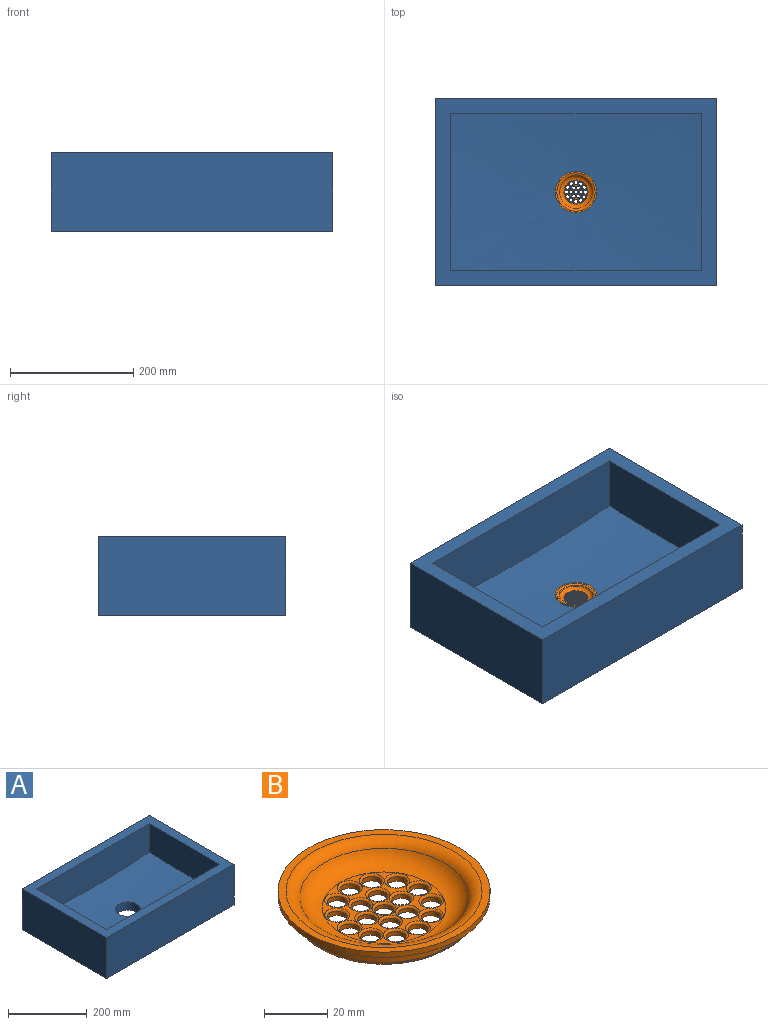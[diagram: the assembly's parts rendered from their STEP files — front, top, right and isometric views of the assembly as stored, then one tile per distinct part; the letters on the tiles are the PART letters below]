
ASSEMBLY  parts=2 mates=1
PART A: 12 faces, bbox 479x479x127 mm
  f0: plane 457.2x304.8mm, normal (0,0,1), area 36129mm2, adj f1,f2,f3,f4,f7,f8,f9,f10
  f1: plane 304.8x127mm, normal (1,0,0), area 38709.6mm2, adj f0,f2,f4,f6
  f2: plane 457.2x127mm, normal (0,1,0), area 58064.4mm2, adj f0,f1,f3,f6
  f3: plane 304.8x127mm, normal (-1,0,0), area 38709.6mm2, adj f0,f2,f4,f6
  f4: plane 457.2x127mm, normal (0,-1,0), area 58064.4mm2, adj f0,f1,f3,f6
  f5: cylinder r=31.75mm len=63.5mm, axis (0,0,-1), area 5120.5mm2, adj f6,f11
  f6: plane 457.2x304.8mm, normal (0,0,-1), area 136187.6mm2, adj f1,f2,f3,f4,f5
  f7: plane 254.01x92.25mm, normal (-1,0,0), area 23125.6mm2, adj f0,f8,f10,f11
  f8: plane 406.41x97.88mm, normal (0,-1,0), area 38525.4mm2, adj f0,f7,f9,f11
  f9: plane 254.01x92.25mm, normal (1,0,0), area 23125.6mm2, adj f0,f8,f10,f11
  f10: plane 406.41x97.88mm, normal (0,1,0), area 38525.4mm2, adj f0,f7,f9,f11
  f11: revolved ~479.02x479.02mm, area 100257.1mm2, adj f5,f7,f8,f9,f10
PART B: 47 faces, bbox 75.1x75.1x11 mm
  f0: cylinder r=28.52mm len=57.05mm, axis (0,0,1), area 1001.5mm2, adj f1,f9
  f1: plane 67.21x67.21mm, normal (0,0,-1), area 991.5mm2, adj f0,f2
  f2: cylinder r=33.6mm len=67.21mm, axis (0,0,1), area 429mm2, adj f1,f3
  f3: plane 67.21x67.21mm, normal (0,0,1), area 516mm2, adj f2,f6
  f4: cone r=25.98mm half-angle=88.9deg, axis (0,0,1), area 306.8mm2, adj f7,f28,f29,f30,f31,f32,f33,f34
  f5: plane 54.51x54.51mm, normal (0,0,-1), area 1752.2mm2, adj f8,f9,f10,f11,f12,f13,f14,f15
  f6: torus R=31.06mm, axis (0,0,-1), area 929.6mm2, adj f3,f7
  f7: torus R=19.41mm, axis (0,0,1), area 1269.6mm2, adj f4,f6
  f8: cylinder r=3.05mm len=6.1mm, axis (0,0,-1), area 25.7mm2, adj f5,f46
  f9: torus R=27.25mm, axis (0,0,-1), area 351.7mm2, adj f0,f5
  f10: cylinder r=3.05mm len=6.1mm, axis (0,0,-1), area 28.6mm2, adj f5,f44
  f11: cylinder r=3.05mm len=6.1mm, axis (0,0,-1), area 28.2mm2, adj f5,f32
  f12: cylinder r=3.05mm len=6.1mm, axis (0,0,-1), area 26.9mm2, adj f5,f29
  f13: cylinder r=3.05mm len=6.1mm, axis (0,0,-1), area 27.4mm2, adj f5,f36
  f14: cylinder r=3.05mm len=6.1mm, axis (0,0,-1), area 26.3mm2, adj f5,f38
  f15: cylinder r=3.05mm len=6.1mm, axis (0,0,-1), area 28.1mm2, adj f5,f41
  f16: cylinder r=3.16mm len=6.32mm, axis (0,0,-1), area 32.7mm2, adj f5,f45
  f17: cylinder r=3.16mm len=6.32mm, axis (0,0,-1), area 32.6mm2, adj f5,f33
  f18: cylinder r=3.16mm len=6.32mm, axis (0,0,-1), area 32.6mm2, adj f5,f43
  f19: cylinder r=3.16mm len=6.32mm, axis (0,0,-1), area 32.1mm2, adj f5,f42
  f20: cylinder r=3.16mm len=6.32mm, axis (0,0,-1), area 31.3mm2, adj f5,f40
  f21: cylinder r=3.16mm len=6.32mm, axis (0,0,-1), area 30.4mm2, adj f5,f39
  f22: cylinder r=3.16mm len=6.32mm, axis (0,0,-1), area 29.9mm2, adj f5,f37
  f23: cylinder r=3.16mm len=6.32mm, axis (0,0,-1), area 30.1mm2, adj f5,f35
  f24: cylinder r=3.16mm len=6.32mm, axis (0,0,-1), area 32.2mm2, adj f5,f34
  f25: cylinder r=3.16mm len=6.32mm, axis (0,0,-1), area 31.5mm2, adj f5,f31
  f26: cylinder r=3.16mm len=6.32mm, axis (0,0,-1), area 30.7mm2, adj f5,f30
  f27: cylinder r=3.16mm len=6.32mm, axis (0,0,-1), area 31.3mm2, adj f5,f28
  f28: bspline ~7.86x7.85mm, area 25.8mm2, adj f4,f27
  f29: bspline ~7.63x7.62mm, area 24.9mm2, adj f4,f12,f30
  f30: bspline ~7.86x7.85mm, area 25.8mm2, adj f4,f26,f29
  f31: bspline ~7.86x7.85mm, area 25.8mm2, adj f4,f25
  f32: bspline ~7.63x7.62mm, area 24.9mm2, adj f4,f11,f34
  f33: bspline ~7.86x7.85mm, area 25.8mm2, adj f4,f17,f34
  f34: bspline ~7.86x7.85mm, area 25.8mm2, adj f4,f24,f32,f33
  f35: bspline ~7.86x7.85mm, area 25.8mm2, adj f4,f23
  f36: bspline ~7.63x7.62mm, area 24.9mm2, adj f4,f13,f37
  f37: bspline ~7.84x7.84mm, area 25.8mm2, adj f4,f22,f36
  f38: bspline ~7.63x7.62mm, area 24.9mm2, adj f4,f14,f39
  f39: bspline ~7.86x7.85mm, area 25.8mm2, adj f4,f21,f38
  f40: bspline ~7.86x7.85mm, area 25.8mm2, adj f4,f20
  f41: bspline ~7.63x7.62mm, area 24.9mm2, adj f4,f15,f42
  f42: bspline ~7.86x7.85mm, area 25.8mm2, adj f4,f19,f41
  f43: bspline ~7.86x7.85mm, area 25.8mm2, adj f4,f18
  f44: bspline ~7.61x7.61mm, area 24.9mm2, adj f4,f10,f45
  f45: bspline ~7.86x7.85mm, area 25.8mm2, adj f4,f16,f44
  f46: torus R=3.81mm, axis (0,0,1), area 24.6mm2, adj f4,f8
PLACE A t=(-51.9,5.04,-11.13)mm
PLACE B t=(-4.74,5.04,32.99)mm
MATE fastened B.f0 <-> A.f5  axis (0,0,-1) through (-51.9,5.04,6.92)mm
